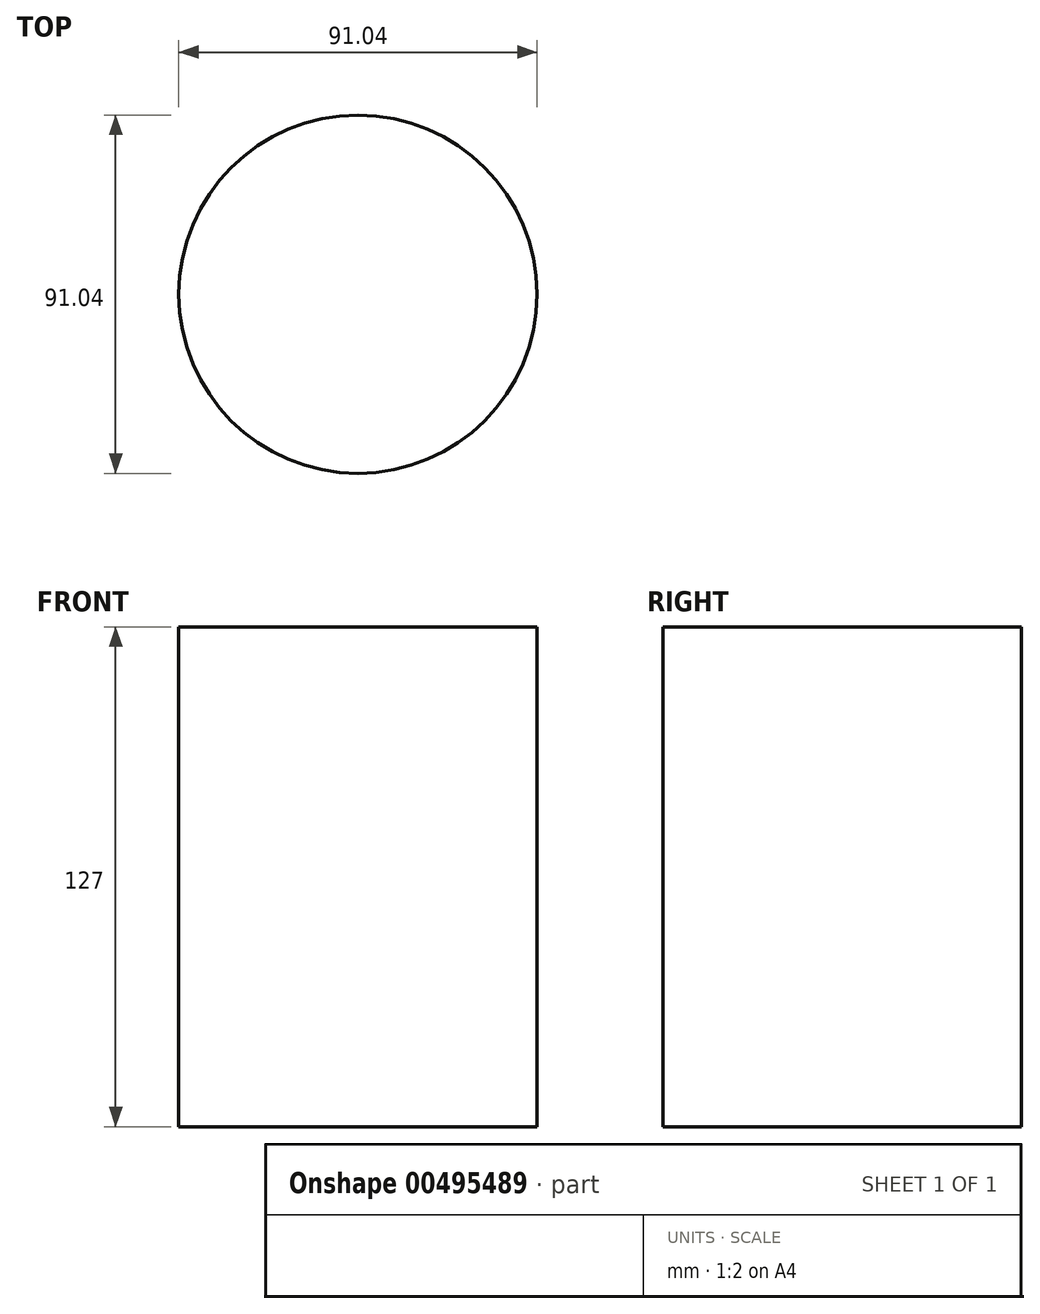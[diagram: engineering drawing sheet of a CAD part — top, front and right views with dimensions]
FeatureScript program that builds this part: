
annotation { "Feature Type Name" : "Feature", "Feature Type Description" : "" }
export const myFeature = defineFeature(function(context is Context, id is Id, definition is map)
    precondition{}
    {
        {
            var Q0;
            Q0=qCreatedBy(makeId("Top.planeOp"),FACE);
            var sketch = newSketch(context, id + "F0", { "sketchPlane" : qUnion([Q0])});
            skCircle(sketch, "E0", {"center": v(0, 0) * mm, "radius": 45.52 * mm});
            skLineSegment(sketch, "E1.bottom", {"start": v(-17.94, 17.74) * mm, "end": v(17.94, 17.74) * mm});
            skLineSegment(sketch, "E1.top", {"start": v(-17.94, -17.74) * mm, "end": v(17.94, -17.74) * mm});
            skLineSegment(sketch, "E1.left", {"start": v(-17.94, 17.74) * mm, "end": v(-17.94, -17.74) * mm});
            skLineSegment(sketch, "E1.right", {"start": v(17.94, 17.74) * mm, "end": v(17.94, -17.74) * mm});
            skSolve(sketch);
        }
        {
            var Q0;
            Q0=sQuery(id+"F0.wireOp",EDGE,"E0");
            extrude(context, id + "F1", {"bodyType" : ToolBodyType.SURFACE, "surfaceEntities" : qUnion([Q0]), "depth" : 127 * mm});
        }
    });
